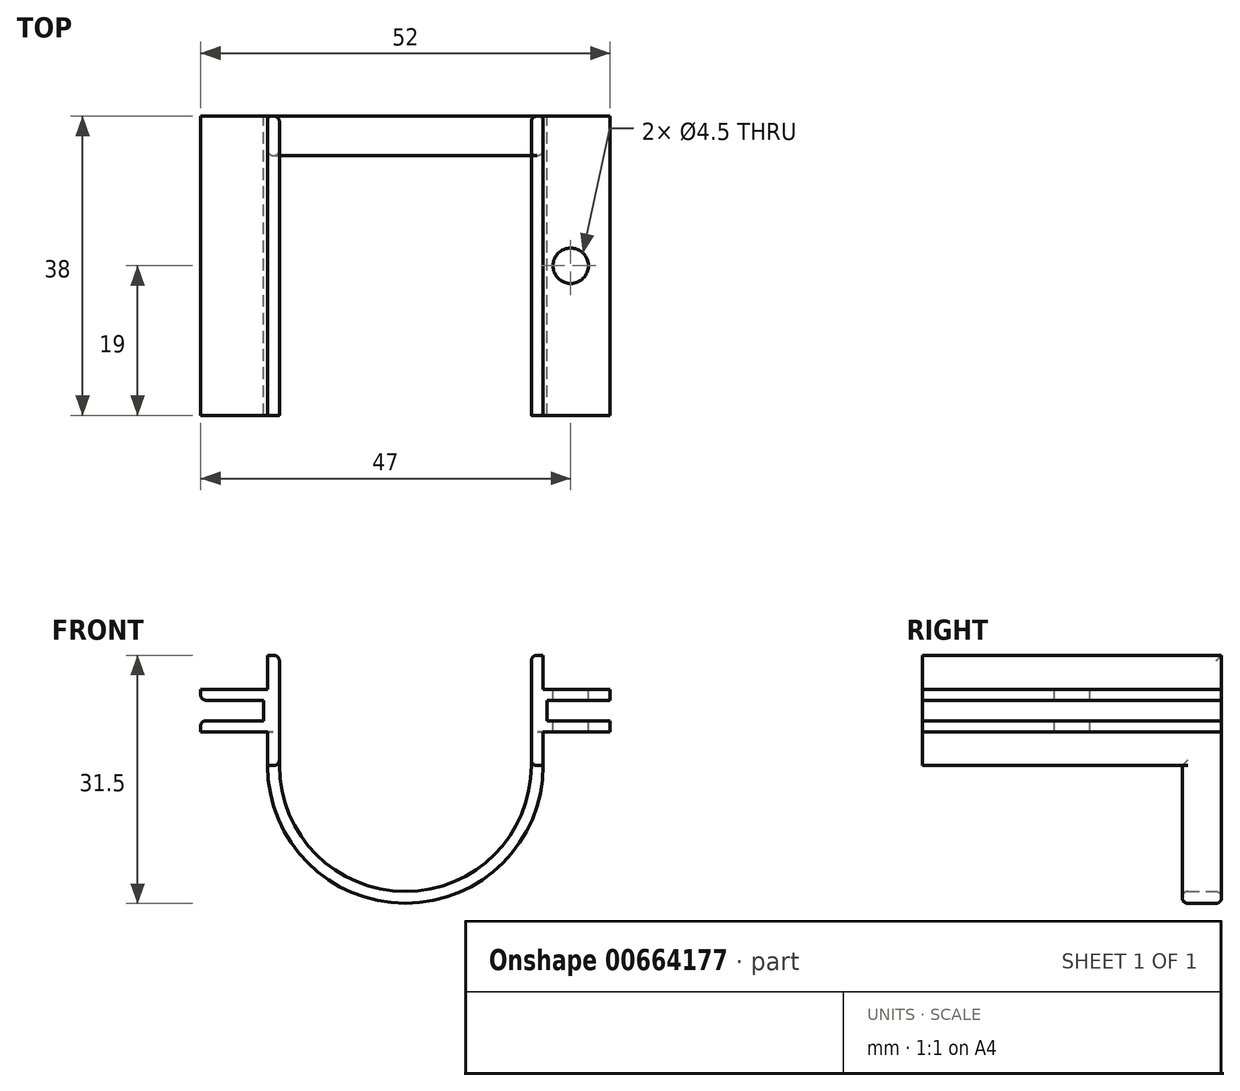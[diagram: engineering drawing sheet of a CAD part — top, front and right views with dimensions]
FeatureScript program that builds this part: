
annotation { "Feature Type Name" : "Feature", "Feature Type Description" : "" }
export const myFeature = defineFeature(function(context is Context, id is Id, definition is map)
    precondition{}
    {
        {
            var Q0;
            Q0=qCreatedBy(makeId("Front.planeOp"),FACE);
            var sketch = newSketch(context, id + "F0", { "sketchPlane" : qUnion([Q0])});
            skCircle(sketch, "E0", {"center": v(0, 0) * mm, "radius": 17.5 * mm});
            skLineSegment(sketch, "E1.bottom", {"start": v(-17.5, 0) * mm, "end": v(-17.5, 0) * mm});
            skLineSegment(sketch, "E1.left", {"start": v(-17.5, 0) * mm, "end": v(-17.5, 0) * mm});
            skLineSegment(sketch, "E2", {"start": v(-17.5, 0) * mm, "end": v(17.5, 0) * mm});
            skSolve(sketch);
        }
        {
            var Q0;
            {var subQ0=sQuery(id+"F0.wireOp",EDGE,"E2");Q0=makeQuery(id+"F0.imprint","IMPRINT",FACE,{"disambiguationData":[TD([[makeQuery(id+"F0.imprint","IMPRINT",EDGE,{"derivedFrom":subQ0}),-1.0]])]});}
            extrude(context, id + "F1", {"entities" : qUnion([Q0]), "depth" : 5 * mm, "offsetDistance" : 25 * mm});
        }
        {
            var Q0;
            Q0=makeQuery(id+"F1.opExtrude","CAP_FACE",FACE,{"disambiguationData":[OSD([sQuery(id+"F0.wireOp",EDGE,"E0"),sQuery(id+"F0.wireOp",EDGE,"E1.top"),sQuery(id+"F0.wireOp",EDGE,"E1.left"),sQuery(id+"F0.wireOp",EDGE,"E1.right"),sQuery(id+"F0.wireOp",EDGE,"LefxOoeR-nq5w-59BA-Ikxv-zXAR8450YXsB.bottom"),sQuery(id+"F0.wireOp",EDGE,"LefxOoeR-nq5w-59BA-Ikxv-zXAR8450YXsB.top"),sQuery(id+"F0.wireOp",EDGE,"LefxOoeR-nq5w-59BA-Ikxv-zXAR8450YXsB.right"),sQuery(id+"F0.wireOp",EDGE,"BH197fx9-mUJi-XVLk-NfY7-dZP8ODIYXxIu.bottom"),sQuery(id+"F0.wireOp",EDGE,"BH197fx9-mUJi-XVLk-NfY7-dZP8ODIYXxIu.top"),sQuery(id+"F0.wireOp",EDGE,"BH197fx9-mUJi-XVLk-NfY7-dZP8ODIYXxIu.right")])],"isStart":false});
            var Q1;
            Q1=makeQuery(id+"F1.opExtrude","SWEPT_FACE",FACE,{"disambiguationData":[OSD([sQuery(id+"F0.wireOp",EDGE,"E1.top"),sQuery(id+"F0.wireOp",EDGE,"LefxOoeR-nq5w-59BA-Ikxv-zXAR8450YXsB.bottom"),sQuery(id+"F0.wireOp",EDGE,"BH197fx9-mUJi-XVLk-NfY7-dZP8ODIYXxIu.bottom")])]});
            var Q2;
            Q2=makeQuery(id+"F1.opExtrude","CAP_FACE",FACE,{"disambiguationData":[OSD([sQuery(id+"F0.wireOp",EDGE,"E0"),sQuery(id+"F0.wireOp",EDGE,"E1.top"),sQuery(id+"F0.wireOp",EDGE,"E1.left"),sQuery(id+"F0.wireOp",EDGE,"E1.right"),sQuery(id+"F0.wireOp",EDGE,"LefxOoeR-nq5w-59BA-Ikxv-zXAR8450YXsB.bottom"),sQuery(id+"F0.wireOp",EDGE,"LefxOoeR-nq5w-59BA-Ikxv-zXAR8450YXsB.top"),sQuery(id+"F0.wireOp",EDGE,"LefxOoeR-nq5w-59BA-Ikxv-zXAR8450YXsB.right"),sQuery(id+"F0.wireOp",EDGE,"BH197fx9-mUJi-XVLk-NfY7-dZP8ODIYXxIu.bottom"),sQuery(id+"F0.wireOp",EDGE,"BH197fx9-mUJi-XVLk-NfY7-dZP8ODIYXxIu.top"),sQuery(id+"F0.wireOp",EDGE,"BH197fx9-mUJi-XVLk-NfY7-dZP8ODIYXxIu.right")])],"isStart":true});
            var Q3;
            Q3=makeQuery(id+"F1.opExtrude","SWEPT_FACE",FACE,{"disambiguationData":[OSD([sQuery(id+"F0.wireOp",EDGE,"E2")])]});
            shell(context, id + "F2", {"entities" : qUnion([Q0, Q1, Q2, Q3]), "thickness" : 1.5 * mm});
        }
        {
            var Q0;
            Q0=qCreatedBy(makeId("Front.planeOp"),FACE);
            var sketch = newSketch(context, id + "F3", { "sketchPlane" : qUnion([Q0])});
            skLineSegment(sketch, "E3.bottom", {"start": v(-16, 0) * mm, "end": v(-26, 0) * mm});
            skLineSegment(sketch, "E3.top", {"start": v(-16, 14) * mm, "end": v(-26, 14) * mm});
            skLineSegment(sketch, "E3.left", {"start": v(-16, 0) * mm, "end": v(-16, 14) * mm});
            skLineSegment(sketch, "E3.right", {"start": v(-26, 0) * mm, "end": v(-26, 14) * mm});
            skLineSegment(sketch, "E4.bottom", {"start": v(-26, 8.3) * mm, "end": v(-18, 8.3) * mm});
            skLineSegment(sketch, "E4.top", {"start": v(-26, 5.7) * mm, "end": v(-18, 5.7) * mm});
            skLineSegment(sketch, "E4.left", {"start": v(-26, 8.3) * mm, "end": v(-26, 5.7) * mm});
            skLineSegment(sketch, "E4.right", {"start": v(-18, 8.3) * mm, "end": v(-18, 5.7) * mm});
            skLineSegment(sketch, "E5.MirrorCS", {"start": v(26, 8.3) * mm, "end": v(26, 5.7) * mm});
            skLineSegment(sketch, "E6.MirrorCS", {"start": v(26, 5.7) * mm, "end": v(18, 5.7) * mm});
            skLineSegment(sketch, "E7.MirrorCS", {"start": v(16, 0) * mm, "end": v(16, 14) * mm});
            skLineSegment(sketch, "E8.MirrorCS", {"start": v(16, 14) * mm, "end": v(26, 14) * mm});
            skLineSegment(sketch, "E9.MirrorCS", {"start": v(26, 8.3) * mm, "end": v(18, 8.3) * mm});
            skLineSegment(sketch, "E10.MirrorCS", {"start": v(16, 0) * mm, "end": v(26, 0) * mm});
            skLineSegment(sketch, "E11.MirrorCS", {"start": v(26, 0) * mm, "end": v(26, 14) * mm});
            skLineSegment(sketch, "E12.MirrorCS", {"start": v(18, 8.3) * mm, "end": v(18, 5.7) * mm});
            skSolve(sketch);
        }
        {
            var Q0;
            {var subQ2=sQuery(id+"F3.wireOp",EDGE,"E6.MirrorCS");Q0=makeQuery(id+"F3.imprint","IMPRINT",FACE,{"disambiguationData":[TD([[makeQuery(id+"F3.imprint","IMPRINT",EDGE,{"derivedFrom":subQ2}),1.0]])]});}
            extrude(context, id + "F4", {"entities" : qUnion([Q0]), "operationType" : NewBodyOperationType.ADD, "depth" : 38 * mm, "offsetDistance" : 25 * mm});
        }
        {
            var Q0;
            {var subQ1=sQuery(id+"F3.wireOp",EDGE,"E3.bottom");Q0=makeQuery(id+"F3.imprint","IMPRINT",FACE,{"disambiguationData":[TD([[makeQuery(id+"F3.imprint","IMPRINT",EDGE,{"derivedFrom":subQ1}),-1.0]])]});}
            var Q1;
            Q1=makeQuery(id+"FaElhSZNQWa5NXD_1.imprint","IMPRINT",FACE,{"disambiguationData":[TD([[makeQuery(id+"FaElhSZNQWa5NXD_1.imprint","IMPRINT",EDGE,{"derivedFrom":sQuery(id+"FaElhSZNQWa5NXD_1.wireOp",EDGE,"CecRilpU-Kbwj-TjNc-GfqX-46ULoclHl2qS.bottom")}),1.0]])]});
            var Q2;
            Q2=makeQuery(id+"FaElhSZNQWa5NXD_1.imprint","IMPRINT",FACE,{"disambiguationData":[TD([[makeQuery(id+"FaElhSZNQWa5NXD_1.imprint","IMPRINT",EDGE,{"derivedFrom":sQuery(id+"FaElhSZNQWa5NXD_1.wireOp",EDGE,"HC3l6eys-JtjY-h8UD-tSyZ-PQuBtLLJUGgb.bottom")}),-1.0]])]});
            var Q3;
            Q3=makeQuery(id+"F4.opExtrude","CAP_FACE",FACE,{"disambiguationData":[OSD([sQuery(id+"F3.wireOp",EDGE,"E6.MirrorCS"),sQuery(id+"F3.wireOp",EDGE,"E7.MirrorCS"),sQuery(id+"F3.wireOp",EDGE,"E8.MirrorCS"),sQuery(id+"F3.wireOp",EDGE,"E9.MirrorCS"),sQuery(id+"F3.wireOp",EDGE,"E10.MirrorCS"),sQuery(id+"F3.wireOp",EDGE,"E11.MirrorCS"),sQuery(id+"F3.wireOp",EDGE,"E12.MirrorCS")])],"isStart":false});
            extrude(context, id + "F5", {"entities" : qUnion([Q0, Q1, Q2]), "endBound" : BoundingType.UP_TO_SURFACE, "depth" : 38 * mm, "endBoundEntityFace" : qUnion([Q3]), "offsetDistance" : 25 * mm});
        }
        {
            var Q0;
            Q0=makeQuery(id+"F5.opExtrude","SWEPT_BODY",BODY,{"disambiguationData":[OSD([sQuery(id+"F3.wireOp",EDGE,"E3.bottom"),sQuery(id+"F3.wireOp",EDGE,"E3.top"),sQuery(id+"F3.wireOp",EDGE,"E3.left"),sQuery(id+"F3.wireOp",EDGE,"E3.right"),sQuery(id+"F3.wireOp",EDGE,"E4.bottom"),sQuery(id+"F3.wireOp",EDGE,"E4.top"),sQuery(id+"F3.wireOp",EDGE,"E4.right")])]});
            var Q1;
            Q1=makeQuery(id+"F1.opExtrude","SWEPT_BODY",BODY,{"disambiguationData":[OSD([sQuery(id+"F0.wireOp",EDGE,"E0"),sQuery(id+"F0.wireOp",EDGE,"E2")])]});
            booleanBodies(context, id + "F6", {"operationType" : BooleanOperationType.UNION, "tools" : qUnion([Q0, Q1])});
        }
        {
            var Q0;
            Q0=makeQuery(id+"F4.opExtrude","SWEPT_FACE",FACE,{"disambiguationData":[OSD([sQuery(id+"F3.wireOp",EDGE,"E8.MirrorCS")])]});
            var sketch = newSketch(context, id + "F7", { "sketchPlane" : qUnion([Q0])});
            skCircle(sketch, "E13", {"center": v(21, -19) * mm, "radius": 2.25 * mm});
            skCircle(sketch, "E14.MirrorC", {"center": v(-21, -19) * mm, "radius": 2.25 * mm});
            skSolve(sketch);
        }
        {
            var Q0;
            Q0=makeQuery(id+"F7.imprint","IMPRINT",FACE,{"disambiguationData":[TD([[makeQuery(id+"F7.imprint","IMPRINT",EDGE,{"derivedFrom":sQuery(id+"F7.wireOp",EDGE,"E13")}),1.0]])]});
            var Q1;
            Q1=makeQuery(id+"F7.imprint","IMPRINT",FACE,{"disambiguationData":[TD([[makeQuery(id+"F7.imprint","IMPRINT",EDGE,{"derivedFrom":sQuery(id+"F7.wireOp",EDGE,"E14.MirrorC")}),-1.0]])]});
            extrude(context, id + "F8", {"entities" : qUnion([Q0, Q1]), "operationType" : NewBodyOperationType.REMOVE, "endBound" : BoundingType.THROUGH_ALL, "oppositeDirection" : true, "depth" : 25 * mm, "offsetDistance" : 25 * mm});
        }
        {
            var Q0;
            {var subQ2=sQuery(id+"F3.wireOp",EDGE,"E6.MirrorCS");Q0=makeQuery(id+"F3.imprint","IMPRINT",FACE,{"disambiguationData":[TD([[makeQuery(id+"F3.imprint","IMPRINT",EDGE,{"derivedFrom":subQ2}),1.0]])]});}
            var sketch = newSketch(context, id + "F9", { "sketchPlane" : qUnion([Q0])});
            skLineSegment(sketch, "E15.bottom", {"start": v(17.5, 0) * mm, "end": v(26, 0) * mm});
            skLineSegment(sketch, "E15.top", {"start": v(17.5, 4.3) * mm, "end": v(26, 4.3) * mm});
            skLineSegment(sketch, "E15.left", {"start": v(17.5, 0) * mm, "end": v(17.5, 4.3) * mm});
            skLineSegment(sketch, "E15.right", {"start": v(26, 0) * mm, "end": v(26, 4.3) * mm});
            skLineSegment(sketch, "E16.bottom", {"start": v(26, 14) * mm, "end": v(17.5, 14) * mm});
            skLineSegment(sketch, "E16.top", {"start": v(26, 9.7) * mm, "end": v(17.5, 9.7) * mm});
            skLineSegment(sketch, "E16.left", {"start": v(26, 14) * mm, "end": v(26, 9.7) * mm});
            skLineSegment(sketch, "E16.right", {"start": v(17.5, 14) * mm, "end": v(17.5, 9.7) * mm});
            skLineSegment(sketch, "E17.MirrorCS", {"start": v(-26, 14) * mm, "end": v(-17.5, 14) * mm});
            skLineSegment(sketch, "E18.MirrorCS", {"start": v(-26, 14) * mm, "end": v(-26, 9.7) * mm});
            skLineSegment(sketch, "E19.MirrorCS", {"start": v(-17.5, 4.3) * mm, "end": v(-26, 4.3) * mm});
            skLineSegment(sketch, "E20.MirrorCS", {"start": v(-26, 0) * mm, "end": v(-26, 4.3) * mm});
            skLineSegment(sketch, "E21.MirrorCS", {"start": v(-17.5, 0) * mm, "end": v(-26, 0) * mm});
            skLineSegment(sketch, "E22.MirrorCS", {"start": v(-17.5, 0) * mm, "end": v(-17.5, 4.3) * mm});
            skLineSegment(sketch, "E23.MirrorCS", {"start": v(-17.5, 14) * mm, "end": v(-17.5, 9.7) * mm});
            skLineSegment(sketch, "E24.MirrorCS", {"start": v(-26, 9.7) * mm, "end": v(-17.5, 9.7) * mm});
            skSolve(sketch);
        }
        {
            var Q0;
            Q0=makeQuery(id+"F9.imprint","IMPRINT",FACE,{"disambiguationData":[TD([[makeQuery(id+"F9.imprint","IMPRINT",EDGE,{"derivedFrom":sQuery(id+"F9.wireOp",EDGE,"E15.bottom")}),1.0]])]});
            var Q1;
            Q1=makeQuery(id+"F9.imprint","IMPRINT",FACE,{"disambiguationData":[TD([[makeQuery(id+"F9.imprint","IMPRINT",EDGE,{"derivedFrom":sQuery(id+"F9.wireOp",EDGE,"E16.bottom")}),-1.0]])]});
            var Q2;
            Q2=makeQuery(id+"F9.imprint","IMPRINT",FACE,{"disambiguationData":[TD([[makeQuery(id+"F9.imprint","IMPRINT",EDGE,{"derivedFrom":sQuery(id+"F9.wireOp",EDGE,"E17.MirrorCS")}),-1.0]])]});
            var Q3;
            Q3=makeQuery(id+"F9.imprint","IMPRINT",FACE,{"disambiguationData":[TD([[makeQuery(id+"F9.imprint","IMPRINT",EDGE,{"derivedFrom":sQuery(id+"F9.wireOp",EDGE,"E19.MirrorCS")}),1.0]])]});
            extrude(context, id + "F10", {"entities" : qUnion([Q0, Q1, Q2, Q3]), "operationType" : NewBodyOperationType.REMOVE, "endBound" : BoundingType.THROUGH_ALL, "depth" : 25 * mm, "offsetDistance" : 25 * mm});
        }
        {
            var Q0;
            {var subQ0=sQuery(id+"F0.wireOp",EDGE,"E0");Q0=makeQuery(id+"F2.opShell","OFFSET_EDGE",EDGE,{"disambiguationData":[OSD([subQ0]),TDD([makeQuery(id+"F1.opExtrude","CAP_EDGE",EDGE,{"disambiguationData":[OSD([subQ0])],"isStart":false})])]});}
            var Q1;
            {var subQ0=sQuery(id+"F0.wireOp",EDGE,"E0");Q1=makeQuery(id+"F2.opShell","OFFSET_EDGE",EDGE,{"disambiguationData":[OSD([subQ0]),TDD([makeQuery(id+"F1.opExtrude","CAP_EDGE",EDGE,{"disambiguationData":[OSD([subQ0])],"isStart":true})])]});}
            var Q2;
            Q2=makeQuery(id+"F10.boolean.opBoolean","COPY",EDGE,{"derivedFrom":makeQuery(id+"F10.opExtrude","SWEPT_EDGE",EDGE,{"disambiguationData":[OSD([sQuery(id+"F3.wireOp",EDGE,"E11.MirrorCS"),sQuery(id+"F9.wireOp",EDGE,"E15.top"),sQuery(id+"F9.wireOp",EDGE,"E15.right")])]})});
            var Q3;
            Q3=makeQuery(id+"F10.boolean.opBoolean","COPY",EDGE,{"derivedFrom":makeQuery(id+"F10.opExtrude","SWEPT_EDGE",EDGE,{"disambiguationData":[OSD([sQuery(id+"F3.wireOp",EDGE,"E10.MirrorCS"),sQuery(id+"F9.wireOp",EDGE,"E15.bottom"),sQuery(id+"F9.wireOp",EDGE,"E15.left")])]})});
            var Q4;
            Q4=makeQuery(id+"F1.opExtrude","CAP_EDGE",EDGE,{"disambiguationData":[OSD([sQuery(id+"F0.wireOp",EDGE,"E0")])],"isStart":false});
            var Q5;
            Q5=makeQuery(id+"Fal6JQNbVcECeyx_1.boolean.opBoolean","COPY",EDGE,{"derivedFrom":makeQuery(id+"Fal6JQNbVcECeyx_1.opExtrude","SWEPT_EDGE",EDGE,{"disambiguationData":[OSD([sQuery(id+"F3.wireOp",EDGE,"E3.right"),sQuery(id+"FaElhSZNQWa5NXD_1.wireOp",EDGE,"HC3l6eys-JtjY-h8UD-tSyZ-PQuBtLLJUGgb.top"),sQuery(id+"FaElhSZNQWa5NXD_1.wireOp",EDGE,"HC3l6eys-JtjY-h8UD-tSyZ-PQuBtLLJUGgb.left")])]})});
            var Q6;
            Q6=makeQuery(id+"F1.opExtrude","CAP_EDGE",EDGE,{"disambiguationData":[OSD([sQuery(id+"F0.wireOp",EDGE,"E0")])],"isStart":true});
            var Q7;
            Q7=makeQuery(id+"F10.boolean.opBoolean","COPY",EDGE,{"derivedFrom":makeQuery(id+"F10.opExtrude","SWEPT_EDGE",EDGE,{"disambiguationData":[OSD([sQuery(id+"F3.wireOp",EDGE,"E8.MirrorCS"),sQuery(id+"F9.wireOp",EDGE,"E16.bottom"),sQuery(id+"F9.wireOp",EDGE,"E16.right")])]})});
            var Q8;
            Q8=makeQuery(id+"Fal6JQNbVcECeyx_1.boolean.opBoolean","COPY",EDGE,{"derivedFrom":makeQuery(id+"Fal6JQNbVcECeyx_1.opExtrude","SWEPT_EDGE",EDGE,{"disambiguationData":[OSD([sQuery(id+"F3.wireOp",EDGE,"E3.right"),sQuery(id+"FaElhSZNQWa5NXD_1.wireOp",EDGE,"CecRilpU-Kbwj-TjNc-GfqX-46ULoclHl2qS.top"),sQuery(id+"FaElhSZNQWa5NXD_1.wireOp",EDGE,"CecRilpU-Kbwj-TjNc-GfqX-46ULoclHl2qS.left")])]})});
            var Q9;
            Q9=makeQuery(id+"F10.boolean.opBoolean","COPY",EDGE,{"derivedFrom":makeQuery(id+"F10.opExtrude","SWEPT_EDGE",EDGE,{"disambiguationData":[OSD([sQuery(id+"F3.wireOp",EDGE,"E11.MirrorCS"),sQuery(id+"F9.wireOp",EDGE,"E16.top"),sQuery(id+"F9.wireOp",EDGE,"E16.left")])]})});
            var Q10;
            Q10=makeQuery(id+"F4.opExtrude","SWEPT_EDGE",EDGE,{"disambiguationData":[OSD([sQuery(id+"F3.wireOp",EDGE,"E7.MirrorCS"),sQuery(id+"F3.wireOp",EDGE,"E8.MirrorCS")])]});
            var Q11;
            Q11=makeQuery(id+"F4.boolean.opBoolean","SPLIT",EDGE,{"derivedFrom":makeQuery(id+"F4.opExtrude","SWEPT_EDGE",EDGE,{"disambiguationData":[OSD([sQuery(id+"F3.wireOp",EDGE,"E7.MirrorCS"),sQuery(id+"F3.wireOp",EDGE,"E10.MirrorCS")])]})});
            var Q12;
            Q12=makeQuery(id+"F10.boolean.opBoolean","COPY",EDGE,{"derivedFrom":makeQuery(id+"F10.opExtrude","SWEPT_EDGE",EDGE,{"disambiguationData":[OSD([sQuery(id+"F9.wireOp",EDGE,"E21.MirrorCS"),sQuery(id+"F9.wireOp",EDGE,"E22.MirrorCS")])]})});
            var Q13;
            Q13=makeQuery(id+"F6.opBoolean","SPLIT",EDGE,{"derivedFrom":makeQuery(id+"F5.opExtrude","SWEPT_EDGE",EDGE,{"disambiguationData":[OSD([sQuery(id+"F3.wireOp",EDGE,"E3.bottom"),sQuery(id+"F3.wireOp",EDGE,"E3.left")])]})});
            var Q14;
            Q14=makeQuery(id+"F10.boolean.opBoolean","COPY",EDGE,{"derivedFrom":makeQuery(id+"F10.opExtrude","SWEPT_EDGE",EDGE,{"disambiguationData":[OSD([sQuery(id+"F9.wireOp",EDGE,"E17.MirrorCS"),sQuery(id+"F9.wireOp",EDGE,"E23.MirrorCS")])]})});
            var Q15;
            Q15=makeQuery(id+"F5.opExtrude","SWEPT_EDGE",EDGE,{"disambiguationData":[OSD([sQuery(id+"F3.wireOp",EDGE,"E3.top"),sQuery(id+"F3.wireOp",EDGE,"E3.left")])]});
            var Q16;
            Q16=makeQuery(id+"F10.boolean.opBoolean","COPY",EDGE,{"derivedFrom":makeQuery(id+"F10.opExtrude","SWEPT_EDGE",EDGE,{"disambiguationData":[OSD([sQuery(id+"F9.wireOp",EDGE,"E19.MirrorCS"),sQuery(id+"F9.wireOp",EDGE,"E20.MirrorCS")])]})});
            var Q17;
            Q17=makeQuery(id+"F5.opExtrude","SWEPT_EDGE",EDGE,{"disambiguationData":[OSD([sQuery(id+"F3.wireOp",EDGE,"E3.right"),sQuery(id+"F3.wireOp",EDGE,"E4.top"),sQuery(id+"F3.wireOp",EDGE,"E4.left")])]});
            var Q18;
            Q18=makeQuery(id+"F5.opExtrude","SWEPT_EDGE",EDGE,{"disambiguationData":[OSD([sQuery(id+"F3.wireOp",EDGE,"E3.right"),sQuery(id+"F3.wireOp",EDGE,"E4.bottom"),sQuery(id+"F3.wireOp",EDGE,"E4.left")])]});
            var Q19;
            Q19=makeQuery(id+"F10.boolean.opBoolean","COPY",EDGE,{"derivedFrom":makeQuery(id+"F10.opExtrude","SWEPT_EDGE",EDGE,{"disambiguationData":[OSD([sQuery(id+"F9.wireOp",EDGE,"E18.MirrorCS"),sQuery(id+"F9.wireOp",EDGE,"E24.MirrorCS")])]})});
            fillet(context, id + "F11", {"entities" : qUnion([Q0, Q1, Q2, Q3, Q4, Q5, Q6, Q7, Q8, Q9, Q10, Q11, Q12, Q13, Q14, Q15, Q16, Q17, Q18, Q19]), "radius" : 0.7 * mm, "tangentPropagation" : true, "allowEdgeOverflow" : false});
        }
    });
